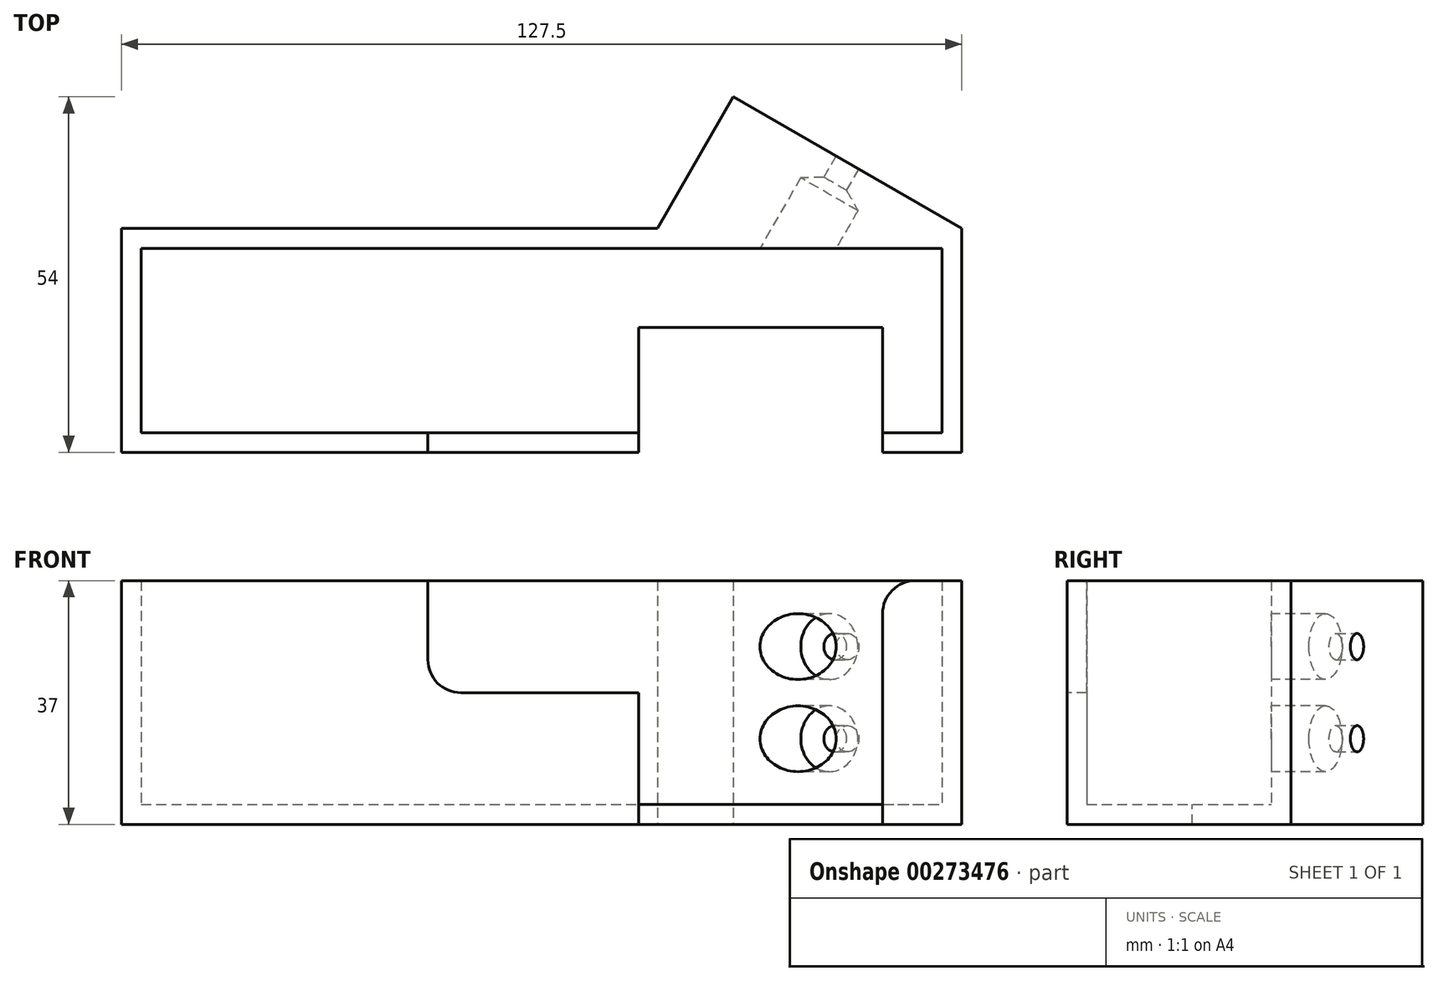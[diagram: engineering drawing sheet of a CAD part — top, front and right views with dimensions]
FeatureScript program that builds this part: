
annotation { "Feature Type Name" : "Feature", "Feature Type Description" : "" }
export const myFeature = defineFeature(function(context is Context, id is Id, definition is map)
    precondition{}
    {
        {
            var Q0;
            Q0=qCreatedBy(makeId("Top.planeOp"),FACE);
            var sketch = newSketch(context, id + "F0", { "sketchPlane" : qUnion([Q0])});
            skLineSegment(sketch, "E0.bottom", {"start": v(0, 0) * mm, "end": v(75.5, 0) * mm});
            skLineSegment(sketch, "E0.top", {"start": v(0, 28) * mm, "end": v(121.5, 28) * mm});
            skLineSegment(sketch, "E0.left", {"start": v(0, 0) * mm, "end": v(0, 28) * mm});
            skLineSegment(sketch, "E0.right", {"start": v(121.5, 0) * mm, "end": v(121.5, 28) * mm});
            skLineSegment(sketch, "E1.0", {"start": v(-3, 31) * mm, "end": v(78.31, 31) * mm});
            skLineSegment(sketch, "E1.1", {"start": v(-3, -3) * mm, "end": v(-3, 31) * mm});
            skLineSegment(sketch, "E1.2", {"start": v(-3, -3) * mm, "end": v(124.5, -3) * mm});
            skLineSegment(sketch, "E1.3", {"start": v(124.5, -3) * mm, "end": v(124.5, 31) * mm});
            skLineSegment(sketch, "E2", {"start": v(112.5, 0) * mm, "end": v(112.5, -3) * mm});
            skLineSegment(sketch, "E3", {"start": v(75.5, 0) * mm, "end": v(75.5, -3) * mm});
            skLineSegment(sketch, "E4.trimOffspring", {"start": v(112.5, 0) * mm, "end": v(121.5, 0) * mm});
            skLineSegment(sketch, "E5", {"start": v(75.5, 0) * mm, "end": v(75.5, 16) * mm});
            skLineSegment(sketch, "E6", {"start": v(75.5, 16) * mm, "end": v(112.5, 16) * mm});
            skLineSegment(sketch, "E7", {"start": v(112.5, 16) * mm, "end": v(112.5, 0) * mm});
            skLineSegment(sketch, "E8", {"start": v(124.5, 31) * mm, "end": v(89.86, 51) * mm});
            skLineSegment(sketch, "E9", {"start": v(89.86, 51) * mm, "end": v(78.31, 31) * mm});
            skSolve(sketch);
        }
        {
            var Q0;
            Q0=makeQuery(id+"F0.imprint","IMPRINT",FACE,{"disambiguationData":[TD([[makeQuery(id+"F0.imprint","IMPRINT",EDGE,{"derivedFrom":sQuery(id+"F0.wireOp",EDGE,"E0.bottom")}),-1.0]])]});
            extrude(context, id + "F1", {"entities" : qUnion([Q0]), "depth" : 34 * mm});
        }
        {
            var Q0;
            Q0=makeQuery(id+"F0.imprint","IMPRINT",FACE,{"disambiguationData":[TD([[makeQuery(id+"F0.imprint","IMPRINT",EDGE,{"derivedFrom":sQuery(id+"F0.wireOp",EDGE,"E0.bottom")}),1.0]])]});
            var Q1;
            Q1=makeQuery(id+"F0.imprint","IMPRINT",FACE,{"disambiguationData":[TD([[makeQuery(id+"F0.imprint","IMPRINT",EDGE,{"derivedFrom":sQuery(id+"F0.wireOp",EDGE,"E0.bottom")}),-1.0]])]});
            extrude(context, id + "F2", {"entities" : qUnion([Q0, Q1]), "operationType" : NewBodyOperationType.ADD, "oppositeDirection" : true, "depth" : 3 * mm});
        }
        {
            var Q0;
            {var subQ0=sQuery(id+"F0.wireOp",EDGE,"E1.2");var subQ1=makeQuery(id+"F0.imprint","IMPRINT",EDGE,{"disambiguationData":[TD([[makeQuery(id+"F0.imprint","INTERSECT",VERTEX,{"derivedFrom":[sQuery(id+"F0.wireOp",EDGE,"E1.1"),subQ0]}),-1.0]])],"derivedFrom":subQ0});Q0=makeQuery(id+"F2.boolean.opBoolean","MERGE",FACE,{"derivedFrom":[makeQuery(id+"F1.opExtrude","SWEPT_FACE",FACE,{"disambiguationData":[OSD([subQ0]),TDD([subQ1])]}),makeQuery(id+"F2.opExtrude","SWEPT_FACE",FACE,{"disambiguationData":[OSD([subQ0]),TDD([subQ1])]})]});}
            var sketch = newSketch(context, id + "F3", { "sketchPlane" : qUnion([Q0])});
            skLineSegment(sketch, "E10", {"start": v(75.5, 17) * mm, "end": v(43.5, 17) * mm});
            skLineSegment(sketch, "E11", {"start": v(43.5, 17) * mm, "end": v(43.5, 34) * mm});
            skSolve(sketch);
        }
        {
            var Q0;
            {var subQ0=sQuery(id+"F3.wireOp",EDGE,"E10");Q0=makeQuery(id+"F3.imprint","IMPRINT",FACE,{"disambiguationData":[TD([[makeQuery(id+"F3.imprint","IMPRINT",EDGE,{"derivedFrom":subQ0}),-1.0]])]});}
            extrude(context, id + "F4", {"entities" : qUnion([Q0]), "operationType" : NewBodyOperationType.REMOVE, "endBound" : BoundingType.UP_TO_NEXT, "oppositeDirection" : true, "depth" : 25 * mm});
        }
        {
            var Q0;
            {var subQ0=sQuery(id+"F0.wireOp",EDGE,"E8");Q0=makeQuery(id+"F2.boolean.opBoolean","MERGE",FACE,{"derivedFrom":[makeQuery(id+"F1.opExtrude","SWEPT_FACE",FACE,{"disambiguationData":[OSD([subQ0])]}),makeQuery(id+"F2.opExtrude","SWEPT_FACE",FACE,{"disambiguationData":[OSD([subQ0])]})]});}
            var sketch = newSketch(context, id + "F5", { "sketchPlane" : qUnion([Q0])});
            skPoint(sketch, "E12", {"position": v(-72.32, 24) * mm});
            skPoint(sketch, "E12.positionSnap0", {"position": v(-72.32, 34) * mm});
            skPoint(sketch, "E13", {"position": v(-72.32, 10) * mm});
            skPoint(sketch, "E13.positionSnap0", {"position": v(-72.32, -3) * mm});
            skSolve(sketch);
        }
        {
            var Q0;
            Q0=sQuery(id+"F5.wireOp",VERTEX,"E12");
            var Q1;
            Q1=sQuery(id+"F5.wireOp",VERTEX,"E13");
            var Q2;
            Q2=makeQuery(id+"F1.opExtrude","SWEPT_BODY",BODY,{"disambiguationData":[OSD([sQuery(id+"F0.wireOp",EDGE,"E0.bottom"),sQuery(id+"F0.wireOp",EDGE,"E0.top"),sQuery(id+"F0.wireOp",EDGE,"E0.left"),sQuery(id+"F0.wireOp",EDGE,"E0.right"),sQuery(id+"F0.wireOp",EDGE,"E1.0"),sQuery(id+"F0.wireOp",EDGE,"E1.1"),sQuery(id+"F0.wireOp",EDGE,"E1.2"),sQuery(id+"F0.wireOp",EDGE,"E1.3"),sQuery(id+"F0.wireOp",EDGE,"E2"),sQuery(id+"F0.wireOp",EDGE,"E3"),sQuery(id+"F0.wireOp",EDGE,"E4.trimOffspring"),sQuery(id+"F0.wireOp",EDGE,"E8"),sQuery(id+"F0.wireOp",EDGE,"E9")])]});
            hole(context, id + "F6", {"style" : HoleStyle.SIMPLE, "endStyle" : HoleEndStyle.THROUGH, "holeDiameter" : 4 * mm, "tappedDepth" : 12 * mm, "tapClearance" : 3, "locations" : qUnion([Q0, Q1]), "scope" : qUnion([Q2])});
        }
        {
            var Q0;
            {var subQ0=sQuery(id+"F0.wireOp",EDGE,"E8");Q0=makeQuery(id+"F2.boolean.opBoolean","MERGE",FACE,{"derivedFrom":[makeQuery(id+"F1.opExtrude","SWEPT_FACE",FACE,{"disambiguationData":[OSD([subQ0])]}),makeQuery(id+"F2.opExtrude","SWEPT_FACE",FACE,{"disambiguationData":[OSD([subQ0])]})]});}
            cPlane(context, id + "F7", {"entities" : qUnion([Q0]), "cplaneType" : CPlaneType.OFFSET, "offset" : 20.8 * mm, "oppositeDirection" : true, "width" : 150 * mm, "height" : 150 * mm});
        }
        {
            var Q0;
            Q0=qCreatedBy(id+"F7.planeOp",FACE);
            var sketch = newSketch(context, id + "F8", { "sketchPlane" : qUnion([Q0])});
            skPoint(sketch, "E14.0", {"position": v(-72.32, 24) * mm});
            skPoint(sketch, "E15.0", {"position": v(-72.32, 10) * mm});
            skSolve(sketch);
        }
        {
            var Q0;
            Q0=sQuery(id+"F8.wireOp",VERTEX,"E14.0");
            var Q1;
            Q1=sQuery(id+"F8.wireOp",VERTEX,"E15.0");
            var Q2;
            Q2=makeQuery(id+"F1.opExtrude","SWEPT_BODY",BODY,{"disambiguationData":[OSD([sQuery(id+"F0.wireOp",EDGE,"E0.bottom"),sQuery(id+"F0.wireOp",EDGE,"E0.top"),sQuery(id+"F0.wireOp",EDGE,"E0.left"),sQuery(id+"F0.wireOp",EDGE,"E0.right"),sQuery(id+"F0.wireOp",EDGE,"E1.0"),sQuery(id+"F0.wireOp",EDGE,"E1.1"),sQuery(id+"F0.wireOp",EDGE,"E1.2"),sQuery(id+"F0.wireOp",EDGE,"E1.3"),sQuery(id+"F0.wireOp",EDGE,"E2"),sQuery(id+"F0.wireOp",EDGE,"E3"),sQuery(id+"F0.wireOp",EDGE,"E4.trimOffspring"),sQuery(id+"F0.wireOp",EDGE,"E8"),sQuery(id+"F0.wireOp",EDGE,"E9")])]});
            hole(context, id + "F9", {"style" : HoleStyle.SIMPLE, "endStyle" : HoleEndStyle.BLIND, "oppositeDirection" : true, "holeDiameter" : 10 * mm, "holeDepth" : 6.6 * mm, "tappedDepth" : 12 * mm, "tapClearance" : 3, "locations" : qUnion([Q0, Q1]), "scope" : qUnion([Q2])});
        }
        {
            var Q0;
            Q0=makeQuery(id+"F1.opExtrude","CAP_EDGE",EDGE,{"disambiguationData":[OSD([sQuery(id+"F0.wireOp",EDGE,"E2")])],"isStart":false});
            var Q1;
            Q1=makeQuery(id+"F4.boolean.opBoolean","COPY",EDGE,{"derivedFrom":makeQuery(id+"F4.opExtrude","SWEPT_EDGE",EDGE,{"disambiguationData":[OSD([sQuery(id+"F0.wireOp",EDGE,"E1.2"),sQuery(id+"F3.wireOp",EDGE,"E11")])]})});
            var Q2;
            Q2=makeQuery(id+"F4.boolean.opBoolean","COPY",EDGE,{"derivedFrom":makeQuery(id+"F4.opExtrude","SWEPT_EDGE",EDGE,{"disambiguationData":[OSD([sQuery(id+"F0.wireOp",EDGE,"E1.2"),sQuery(id+"F0.wireOp",EDGE,"E3"),sQuery(id+"F3.wireOp",EDGE,"E10")])]})});
            var Q3;
            Q3=makeQuery(id+"F4.boolean.opBoolean","COPY",EDGE,{"derivedFrom":makeQuery(id+"F4.opExtrude","SWEPT_EDGE",EDGE,{"disambiguationData":[OSD([sQuery(id+"F3.wireOp",EDGE,"E10"),sQuery(id+"F3.wireOp",EDGE,"E11")])]})});
            fillet(context, id + "F10", {"entities" : qUnion([Q0, Q1, Q2, Q3]), "radius" : 5 * mm, "tangentPropagation" : true, "allowEdgeOverflow" : false});
        }
    });
